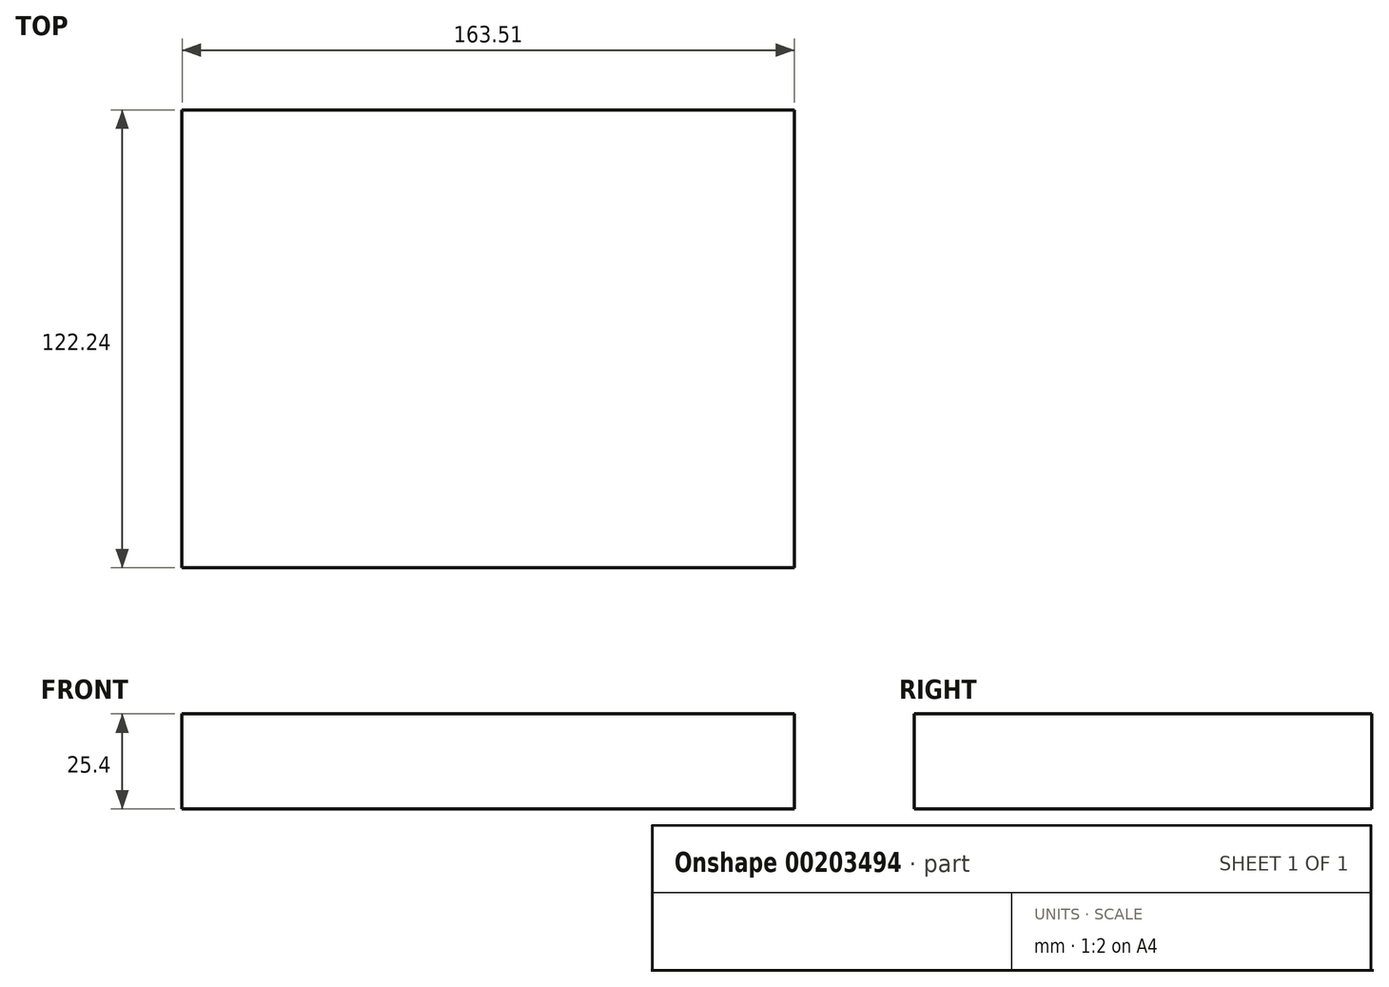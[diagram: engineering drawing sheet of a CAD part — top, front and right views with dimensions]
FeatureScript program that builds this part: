
annotation { "Feature Type Name" : "Feature", "Feature Type Description" : "" }
export const myFeature = defineFeature(function(context is Context, id is Id, definition is map)
    precondition{}
    {
        {
            var Q0;
            Q0=qCreatedBy(makeId("Top.planeOp"),FACE);
            var sketch = newSketch(context, id + "F0", { "sketchPlane" : qUnion([Q0])});
            skLineSegment(sketch, "E0.bottom", {"start": v(-82.9, -55.38) * mm, "end": v(80.61, -55.38) * mm});
            skLineSegment(sketch, "E0.top", {"start": v(-82.9, 66.86) * mm, "end": v(80.61, 66.86) * mm});
            skLineSegment(sketch, "E0.left", {"start": v(-82.9, -55.38) * mm, "end": v(-82.9, 66.86) * mm});
            skLineSegment(sketch, "E0.right", {"start": v(80.61, -55.38) * mm, "end": v(80.61, 66.86) * mm});
            skSolve(sketch);
        }
        {
            var Q0;
            Q0=makeQuery(id+"F0.imprint","IMPRINT",FACE,{"disambiguationData":[TD([[makeQuery(id+"F0.imprint","IMPRINT",EDGE,{"derivedFrom":sQuery(id+"F0.wireOp",EDGE,"E0.bottom")}),1.0]])]});
            extrude(context, id + "F1", {"entities" : qUnion([Q0]), "depth" : 25.4 * mm});
        }
    });
